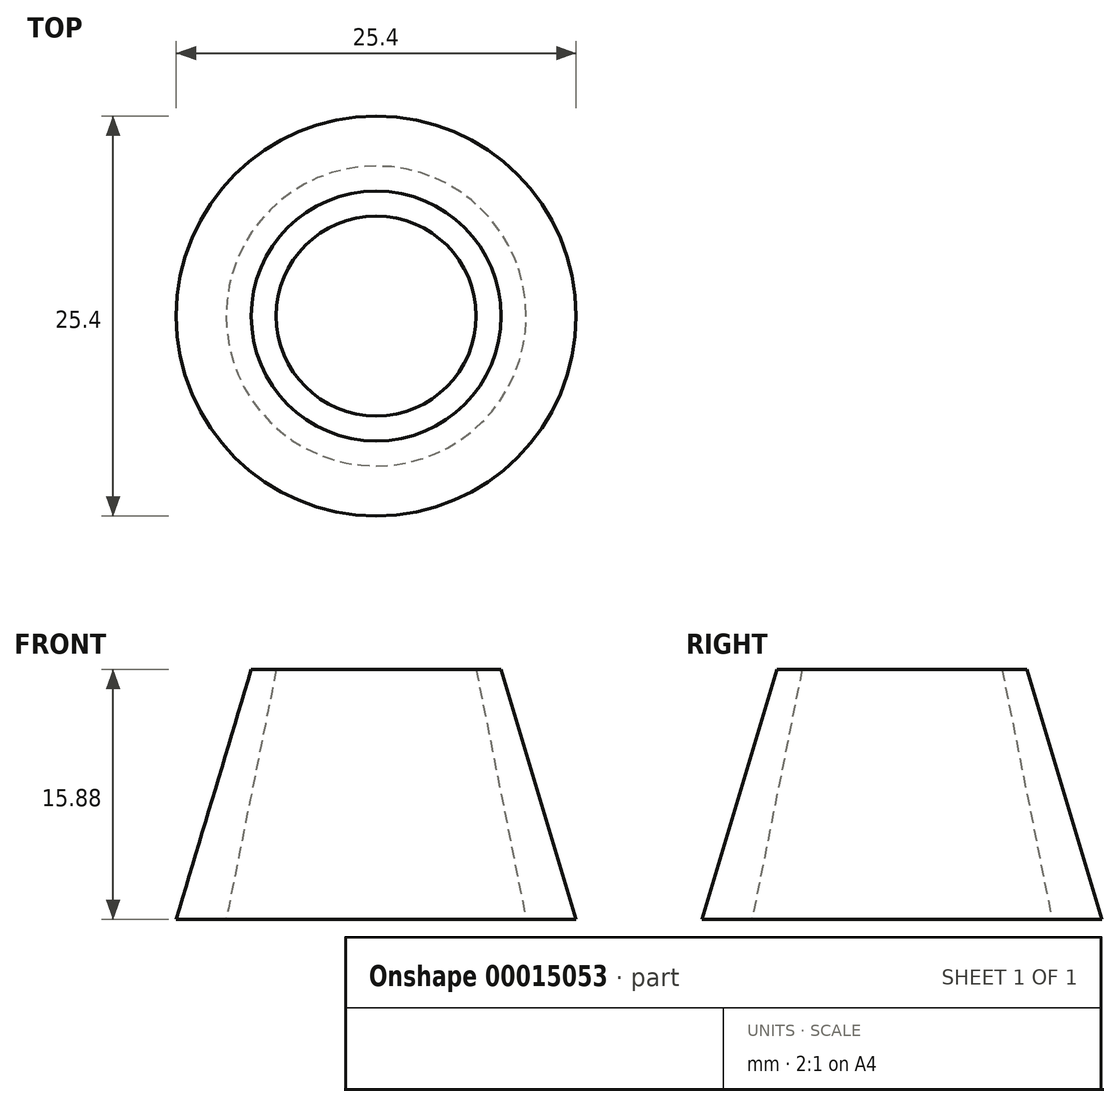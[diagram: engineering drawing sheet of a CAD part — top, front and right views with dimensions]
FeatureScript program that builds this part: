
annotation { "Feature Type Name" : "Feature", "Feature Type Description" : "" }
export const myFeature = defineFeature(function(context is Context, id is Id, definition is map)
    precondition{}
    {
        {
            var Q0;
            Q0=qCreatedBy(makeId("Right.planeOp"),FACE);
            var sketch = newSketch(context, id + "F0", { "sketchPlane" : qUnion([Q0])});
            skLineSegment(sketch, "E0", {"start": v(6.35, 15.88) * mm, "end": v(7.94, 15.88) * mm});
            skLineSegment(sketch, "E1", {"start": v(7.94, 15.88) * mm, "end": v(12.7, 0) * mm});
            skLineSegment(sketch, "E2", {"start": v(12.7, 0) * mm, "end": v(9.53, 0) * mm});
            skLineSegment(sketch, "E3", {"start": v(9.52, 0) * mm, "end": v(6.35, 15.88) * mm});
            skLineSegment(sketch, "E4", {"start": v(0, 0) * mm, "end": v(0, 15.88) * mm, "construction": true});
            skSolve(sketch);
        }
        {
            var Q0;
            Q0=makeQuery(id+"F0.imprint","IMPRINT",FACE,{"disambiguationData":[TD([[makeQuery(id+"F0.imprint","IMPRINT",EDGE,{"derivedFrom":sQuery(id+"F0.wireOp",EDGE,"E0")}),-1.0]])]});
            var Q1;
            Q1=sQuery(id+"F0.wireOp",EDGE,"E4");
            revolve(context, id + "F1", {"entities" : qUnion([Q0]), "axis" : qUnion([Q1]), "revolveType" : RevolveType.FULL});
        }
    });
